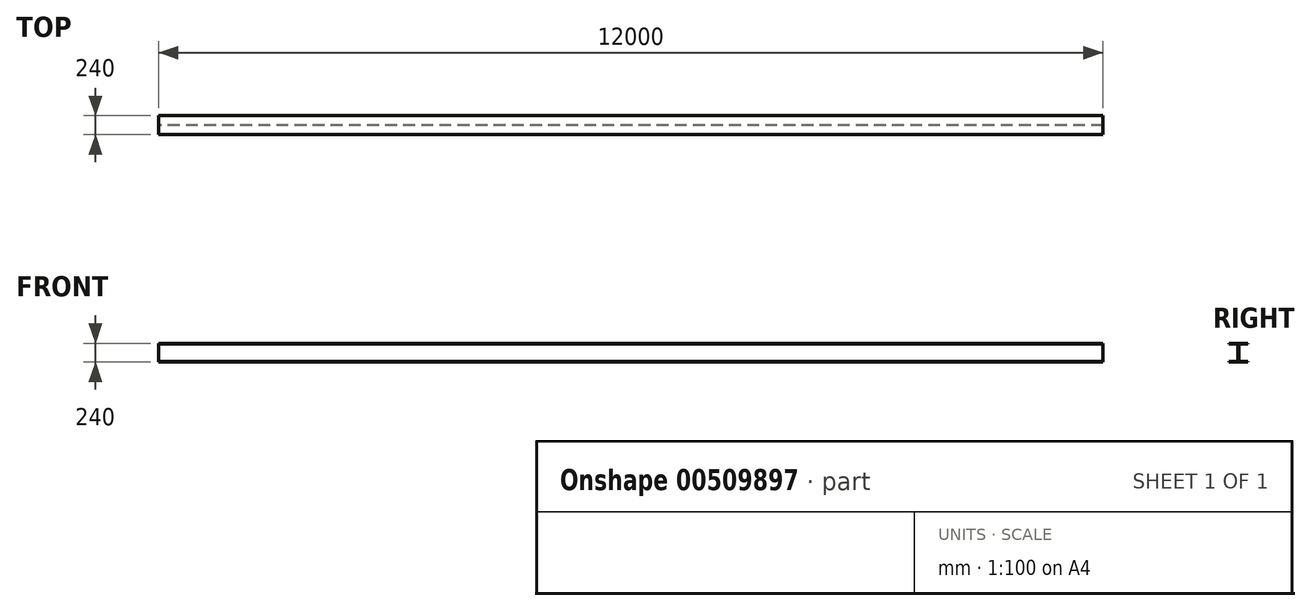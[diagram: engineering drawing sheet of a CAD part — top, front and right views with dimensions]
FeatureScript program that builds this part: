
annotation { "Feature Type Name" : "Feature", "Feature Type Description" : "" }
export const myFeature = defineFeature(function(context is Context, id is Id, definition is map)
    precondition{}
    {
        {
            var Q0;
            Q0=qCreatedBy(makeId("Right.planeOp"),FACE);
            var sketch = newSketch(context, id + "F0", { "sketchPlane" : qUnion([Q0])});
            skLineSegment(sketch, "E0", {"start": v(-44.36, -10) * mm, "end": v(195.64, -10) * mm});
            skLineSegment(sketch, "E1", {"start": v(195.64, -10) * mm, "end": v(195.64, 0) * mm});
            skLineSegment(sketch, "E2", {"start": v(195.64, 0) * mm, "end": v(80.64, 0) * mm});
            skLineSegment(sketch, "E3", {"start": v(80.64, 0) * mm, "end": v(80.64, 220) * mm});
            skLineSegment(sketch, "E4", {"start": v(80.64, 220) * mm, "end": v(195.64, 220) * mm});
            skLineSegment(sketch, "E5", {"start": v(195.64, 220) * mm, "end": v(195.64, 230) * mm});
            skPoint(sketch, "E6.endSnap0", {"position": v(195.64, 225) * mm});
            skLineSegment(sketch, "E7", {"start": v(195.64, 230) * mm, "end": v(-44.36, 230) * mm});
            skLineSegment(sketch, "E8", {"start": v(-44.36, 230) * mm, "end": v(-44.36, 220) * mm});
            skLineSegment(sketch, "E9", {"start": v(-44.36, 220) * mm, "end": v(70.64, 220) * mm});
            skLineSegment(sketch, "E10", {"start": v(70.64, 220) * mm, "end": v(70.64, 0) * mm});
            skLineSegment(sketch, "E11", {"start": v(70.64, 0) * mm, "end": v(-44.36, 0) * mm});
            skLineSegment(sketch, "E12", {"start": v(-44.36, 0) * mm, "end": v(-44.36, -10) * mm});
            skSolve(sketch);
        }
        {
            var Q0;
            Q0=makeQuery(id+"F0.imprint","IMPRINT",FACE,{"disambiguationData":[TD([[makeQuery(id+"F0.imprint","IMPRINT",EDGE,{"derivedFrom":sQuery(id+"F0.wireOp",EDGE,"E0")}),1.0]])]});
            extrude(context, id + "F1", {"entities" : qUnion([Q0]), "depth" : 12000 * mm});
        }
    });
